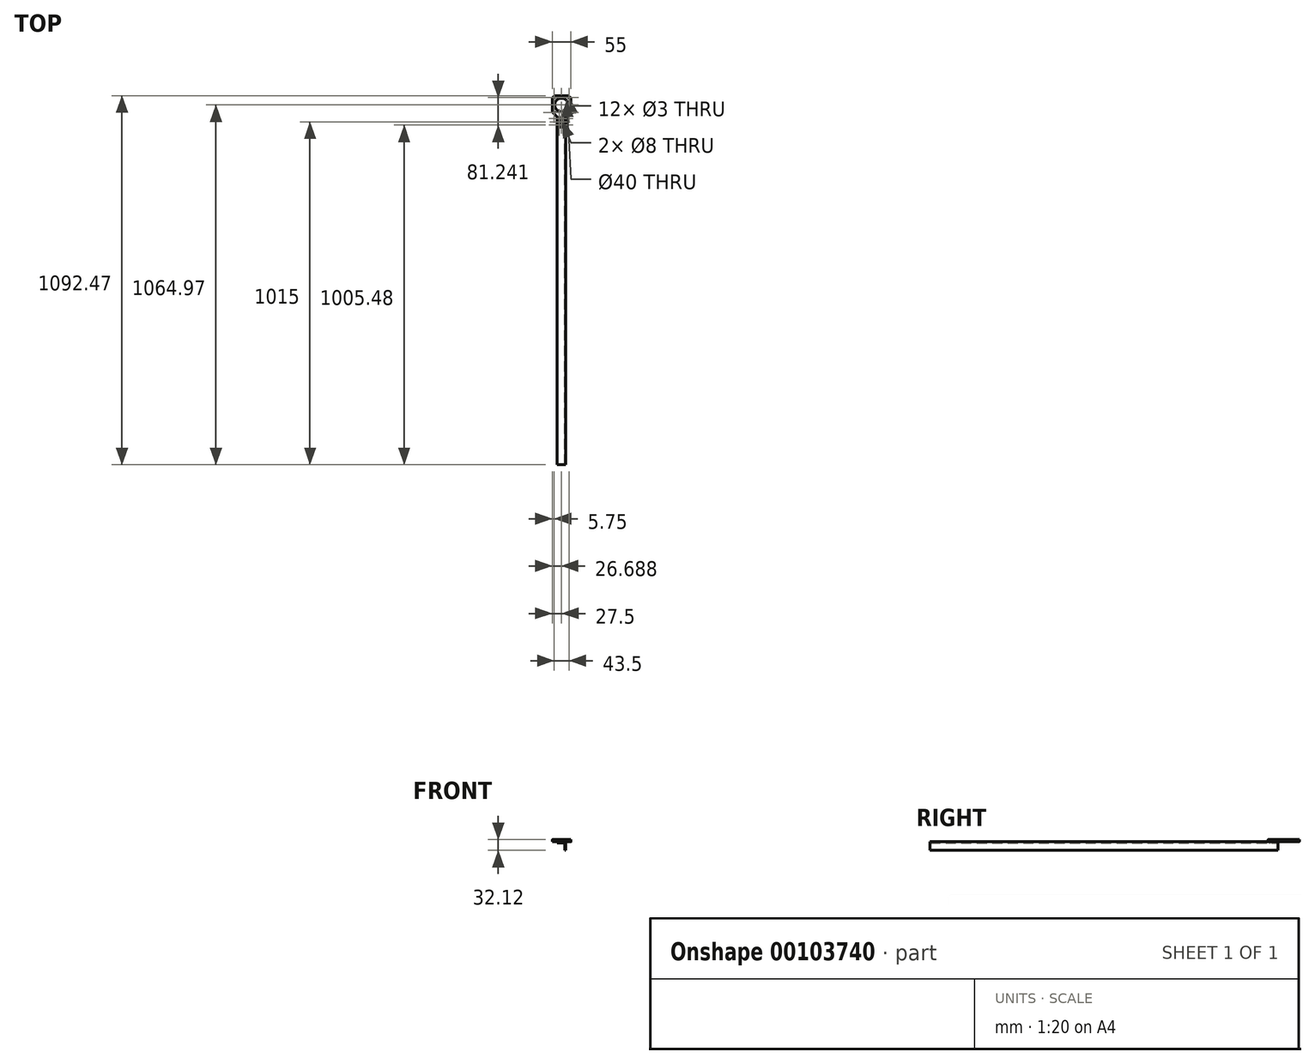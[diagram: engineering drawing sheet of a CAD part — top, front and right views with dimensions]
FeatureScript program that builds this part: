
annotation { "Feature Type Name" : "Feature", "Feature Type Description" : "" }
export const myFeature = defineFeature(function(context is Context, id is Id, definition is map)
    precondition{}
    {
        {
            var Q0;
            Q0=qCreatedBy(makeId("Top.planeOp"),FACE);
            var sketch = newSketch(context, id + "F0", { "sketchPlane" : qUnion([Q0])});
            skLineSegment(sketch, "E0.top", {"start": v(20.23, 27.5) * mm, "end": v(-20.23, 27.5) * mm});
            skLineSegment(sketch, "E0.left", {"start": v(27.5, -20.23) * mm, "end": v(27.5, 20.23) * mm});
            skLineSegment(sketch, "E0.right", {"start": v(-27.5, -20.23) * mm, "end": v(-27.5, 20.23) * mm});
            skPoint(sketch, "E0.middle", {"position": v(0, 0) * mm});
            skCircle(sketch, "E1", {"center": v(0, 0) * mm, "radius": 20 * mm});
            skLineSegment(sketch, "E2.bottom", {"start": v(21.75, -21.75) * mm, "end": v(-21.75, -21.75) * mm, "construction": true});
            skLineSegment(sketch, "E2.top", {"start": v(21.75, 21.75) * mm, "end": v(-21.75, 21.75) * mm, "construction": true});
            skLineSegment(sketch, "E2.left", {"start": v(21.75, -21.75) * mm, "end": v(21.75, 21.75) * mm, "construction": true});
            skLineSegment(sketch, "E2.right", {"start": v(-21.75, -21.75) * mm, "end": v(-21.75, 21.75) * mm, "construction": true});
            skCircle(sketch, "E3", {"center": v(21.75, 21.75) * mm, "radius": 1.5 * mm});
            skCircle(sketch, "E4.MirrorC", {"center": v(21.75, -21.75) * mm, "radius": 1.5 * mm});
            skCircle(sketch, "E5.MirrorC", {"center": v(-21.75, 21.75) * mm, "radius": 1.5 * mm});
            skCircle(sketch, "E6.MirrorC", {"center": v(-21.75, -21.75) * mm, "radius": 1.5 * mm});
            skLineSegment(sketch, "E7", {"start": v(27.5, 20.23) * mm, "end": v(20.23, 27.5) * mm});
            skLineSegment(sketch, "E8", {"start": v(0, 0) * mm, "end": v(27.5, -27.5) * mm, "construction": true});
            skLineSegment(sketch, "E9.MirrorCS", {"start": v(-20.23, -27.5) * mm, "end": v(-27.5, -20.23) * mm});
            skLineSegment(sketch, "E10.MirrorCS", {"start": v(-27.5, 20.23) * mm, "end": v(-20.23, 27.5) * mm});
            skLineSegment(sketch, "E11.MirrorCS", {"start": v(20.23, -27.5) * mm, "end": v(27.5, -20.23) * mm});
            skPoint(sketch, "E12.orphan", {"position": v(-27.5, 27.5) * mm});
            skPoint(sketch, "E13.orphan", {"position": v(-27.5, -27.5) * mm});
            skPoint(sketch, "E14.orphan", {"position": v(27.5, 27.5) * mm});
            skLineSegment(sketch, "E15", {"start": v(-12.76, -34.97) * mm, "end": v(-12.76, -64.97) * mm});
            skLineSegment(sketch, "E16.MirrorCS", {"start": v(12.76, -34.97) * mm, "end": v(12.76, -64.97) * mm});
            skLineSegment(sketch, "E17", {"start": v(-20.23, -27.5) * mm, "end": v(-12.76, -34.97) * mm});
            skLineSegment(sketch, "E18.MirrorCS", {"start": v(20.23, -27.5) * mm, "end": v(12.76, -34.97) * mm});
            skPoint(sketch, "E19.end.orphan", {"position": v(20.23, -64.83) * mm});
            skPoint(sketch, "E20.orphan", {"position": v(-12.76, -27.5) * mm});
            skPoint(sketch, "E21.orphan", {"position": v(12.76, -27.5) * mm});
            skLineSegment(sketch, "E22", {"start": v(12.76, -64.97) * mm, "end": v(-12.76, -64.97) * mm});
            skSolve(sketch);
        }
        {
            var Q0;
            Q0 = qSketchRegion(id + "F0", true);
            extrude(context, id + "F1", {"entities" : qUnion([Q0]), "depth" : 6.6 * mm});
        }
        {
            var Q0;
            Q0=makeQuery(id+"F1.opExtrude","SWEPT_FACE",FACE,{"disambiguationData":[OSD([sQuery(id+"F0.wireOp",EDGE,"E22")])]});
            var sketch = newSketch(context, id + "F2", { "sketchPlane" : qUnion([Q0])});
            skLineSegment(sketch, "E23.1", {"start": v(12.76, 0) * mm, "end": v(-12.76, 0) * mm});
            skLineSegment(sketch, "E24", {"start": v(12.76, 0) * mm, "end": v(12.76, -25.52) * mm});
            skLineSegment(sketch, "E25.0", {"start": v(9.5, -3.25) * mm, "end": v(9.5, -25.52) * mm});
            skLineSegment(sketch, "E25.1", {"start": v(9.5, -3.25) * mm, "end": v(-12.76, -3.25) * mm});
            skLineSegment(sketch, "E26", {"start": v(12.76, -25.52) * mm, "end": v(9.5, -25.52) * mm});
            skLineSegment(sketch, "E27", {"start": v(-12.76, 0) * mm, "end": v(-12.76, -3.25) * mm});
            skPoint(sketch, "E23.0.start.orphan", {"position": v(12.76, 6.6) * mm});
            skPoint(sketch, "E23.2.start.orphan", {"position": v(-12.76, 6.6) * mm});
            skSolve(sketch);
        }
        {
            var Q0;
            Q0 = qSketchRegion(id + "F2", true);
            extrude(context, id + "F3", {"entities" : qUnion([Q0]), "depth" : 1000 * mm, "hasSecondDirection" : true, "secondDirectionOppositeDirection" : true, "secondDirectionDepth" : 30 * mm});
        }
        {
            var Q0;
            Q0=makeQuery(id+"F1.opExtrude","CAP_FACE",FACE,{"disambiguationData":[OSD([sQuery(id+"F0.wireOp",EDGE,"E0.top"),sQuery(id+"F0.wireOp",EDGE,"E0.left"),sQuery(id+"F0.wireOp",EDGE,"E0.right"),sQuery(id+"F0.wireOp",EDGE,"E1"),sQuery(id+"F0.wireOp",EDGE,"E3"),sQuery(id+"F0.wireOp",EDGE,"E4.MirrorC"),sQuery(id+"F0.wireOp",EDGE,"E5.MirrorC"),sQuery(id+"F0.wireOp",EDGE,"E6.MirrorC"),sQuery(id+"F0.wireOp",EDGE,"E7"),sQuery(id+"F0.wireOp",EDGE,"E9.MirrorCS"),sQuery(id+"F0.wireOp",EDGE,"E10.MirrorCS"),sQuery(id+"F0.wireOp",EDGE,"E11.MirrorCS"),sQuery(id+"F0.wireOp",EDGE,"E15"),sQuery(id+"F0.wireOp",EDGE,"E16.MirrorCS"),sQuery(id+"F0.wireOp",EDGE,"E17"),sQuery(id+"F0.wireOp",EDGE,"E18.MirrorCS"),sQuery(id+"F0.wireOp",EDGE,"E22")])],"isStart":false});
            var sketch = newSketch(context, id + "F4", { "sketchPlane" : qUnion([Q0])});
            skLineSegment(sketch, "E28.0", {"start": v(-12.76, -1064.97) * mm, "end": v(-12.76, -34.97) * mm, "construction": true});
            skLineSegment(sketch, "E28.1", {"start": v(9.5, -1064.97) * mm, "end": v(9.5, -34.97) * mm, "construction": true});
            skLineSegment(sketch, "E29", {"start": v(0, -34.97) * mm, "end": v(0, -64.97) * mm, "construction": true});
            skPoint(sketch, "E30.0.start.orphan", {"position": v(9.5, -34.97) * mm});
            skLineSegment(sketch, "E31", {"start": v(-12.76, -34.97) * mm, "end": v(0, -34.97) * mm, "construction": true});
            skCircle(sketch, "E32", {"center": v(-6.38, -40.45) * mm, "radius": 1.5 * mm});
            skPoint(sketch, "E32.centerSnap0", {"position": v(-6.38, -34.97) * mm});
            skLineSegment(sketch, "E33", {"start": v(0, -34.97) * mm, "end": v(9.5, -34.97) * mm, "construction": true});
            skCircle(sketch, "E34", {"center": v(4.75, -40.45) * mm, "radius": 1.5 * mm});
            skPoint(sketch, "E34.centerSnap0", {"position": v(4.75, -34.97) * mm});
            skLineSegment(sketch, "E35", {"start": v(-12.76, -49.97) * mm, "end": v(9.5, -49.97) * mm, "construction": true});
            skPoint(sketch, "E35.endSnap0", {"position": v(0, -49.97) * mm});
            skCircle(sketch, "E36.MirrorC", {"center": v(-6.38, -59.5) * mm, "radius": 1.5 * mm});
            skCircle(sketch, "E37.MirrorC", {"center": v(4.75, -59.5) * mm, "radius": 1.5 * mm});
            skLineSegment(sketch, "E38", {"start": v(-6.38, -40.45) * mm, "end": v(4.75, -40.45) * mm, "construction": true});
            skCircle(sketch, "E39", {"center": v(-0.81, -49.97) * mm, "radius": 4 * mm});
            skPoint(sketch, "E39.centerSnap0", {"position": v(-0.81, -40.45) * mm});
            skSolve(sketch);
        }
        {
            var Q0;
            Q0 = qSketchRegion(id + "F4", true);
            extrude(context, id + "F5", {"entities" : qUnion([Q0]), "operationType" : NewBodyOperationType.REMOVE, "endBound" : BoundingType.THROUGH_ALL, "oppositeDirection" : true, "depth" : 25 * mm});
        }
        {
            var Q0;
            Q0=makeQuery(id+"F1.opExtrude","SWEPT_EDGE",EDGE,{"disambiguationData":[OSD([sQuery(id+"F0.wireOp",EDGE,"E16.MirrorCS"),sQuery(id+"F0.wireOp",EDGE,"E22")])]});
            var Q1;
            Q1=makeQuery(id+"F1.opExtrude","SWEPT_EDGE",EDGE,{"disambiguationData":[OSD([sQuery(id+"F0.wireOp",EDGE,"E15"),sQuery(id+"F0.wireOp",EDGE,"E22")])]});
            var Q2;
            Q2=makeQuery(id+"F1.opExtrude","SWEPT_EDGE",EDGE,{"disambiguationData":[OSD([sQuery(id+"F0.wireOp",EDGE,"E0.left"),sQuery(id+"F0.wireOp",EDGE,"E11.MirrorCS")])]});
            var Q3;
            Q3=makeQuery(id+"F1.opExtrude","SWEPT_EDGE",EDGE,{"disambiguationData":[OSD([sQuery(id+"F0.wireOp",EDGE,"E16.MirrorCS"),sQuery(id+"F0.wireOp",EDGE,"E18.MirrorCS")])]});
            var Q4;
            Q4=makeQuery(id+"F1.opExtrude","SWEPT_EDGE",EDGE,{"disambiguationData":[OSD([sQuery(id+"F0.wireOp",EDGE,"E15"),sQuery(id+"F0.wireOp",EDGE,"E17")])]});
            var Q5;
            Q5=makeQuery(id+"F1.opExtrude","SWEPT_EDGE",EDGE,{"disambiguationData":[OSD([sQuery(id+"F0.wireOp",EDGE,"E0.right"),sQuery(id+"F0.wireOp",EDGE,"E9.MirrorCS")])]});
            var Q6;
            Q6=makeQuery(id+"F1.opExtrude","SWEPT_EDGE",EDGE,{"disambiguationData":[OSD([sQuery(id+"F0.wireOp",EDGE,"E0.left"),sQuery(id+"F0.wireOp",EDGE,"E7")])]});
            var Q7;
            Q7=makeQuery(id+"F1.opExtrude","SWEPT_EDGE",EDGE,{"disambiguationData":[OSD([sQuery(id+"F0.wireOp",EDGE,"E0.top"),sQuery(id+"F0.wireOp",EDGE,"E7")])]});
            var Q8;
            Q8=makeQuery(id+"F1.opExtrude","SWEPT_EDGE",EDGE,{"disambiguationData":[OSD([sQuery(id+"F0.wireOp",EDGE,"E0.top"),sQuery(id+"F0.wireOp",EDGE,"E10.MirrorCS")])]});
            var Q9;
            Q9=makeQuery(id+"F1.opExtrude","SWEPT_EDGE",EDGE,{"disambiguationData":[OSD([sQuery(id+"F0.wireOp",EDGE,"E0.right"),sQuery(id+"F0.wireOp",EDGE,"E10.MirrorCS")])]});
            fillet(context, id + "F6", {"entities" : qUnion([Q0, Q1, Q2, Q3, Q4, Q5, Q6, Q7, Q8, Q9]), "radius" : .5 * mm, "tangentPropagation" : true, "allowEdgeOverflow" : false});
        }
    });
